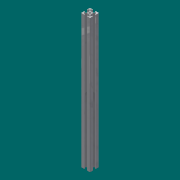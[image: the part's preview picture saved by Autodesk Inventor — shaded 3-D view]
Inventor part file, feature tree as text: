
AUTODESK INVENTOR PART (.ipt)
format: ipt  version: 2016 SP1 (Build 200210100, 210)  size: 147,968 bytes
history: native  units: mm
features: extrude x1, sketch x1
ambient origin geometry x8: Origin, YZ Plane, XZ Plane, XY Plane, X Axis, Y Axis, Z Axis, Center Point
bodies: Solid1 (feature_tree)
feature tree (2):
  extrude  "Extrusion1"  [1 undecoded]
  sketch  "Sketch1"  dims[d0=300.0mm d1=0.0mm]
note: 1 required parameter value undecoded (feature->parameter linkage not recoverable at this tier; creation-order binding heuristic only, values carry confidence <= 0.55)
